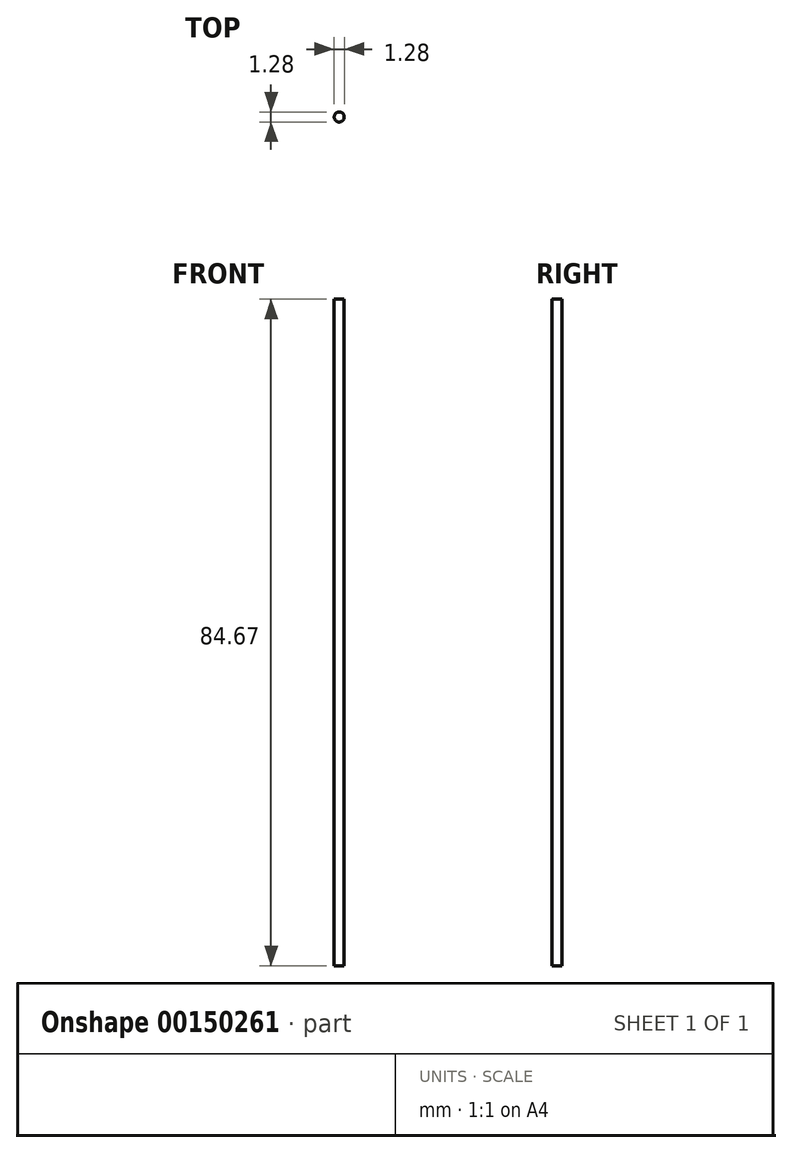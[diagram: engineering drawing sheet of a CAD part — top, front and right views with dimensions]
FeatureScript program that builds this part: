
annotation { "Feature Type Name" : "Feature", "Feature Type Description" : "" }
export const myFeature = defineFeature(function(context is Context, id is Id, definition is map)
    precondition{}
    {
        {
            var Q0;
            Q0=qCreatedBy(makeId("Top.planeOp"),FACE);
            var sketch = newSketch(context, id + "F0", { "sketchPlane" : qUnion([Q0])});
            skCircle(sketch, "E0", {"center": v(0, 0) * mm, "radius": 0.64 * mm});
            skSolve(sketch);
        }
        {
            var Q0;
            Q0=qSketchRegion(id+"F0",true);
            extrude(context, id + "F1", {"entities" : qUnion([Q0]), "depth" : 84.67 * mm});
        }
    });
